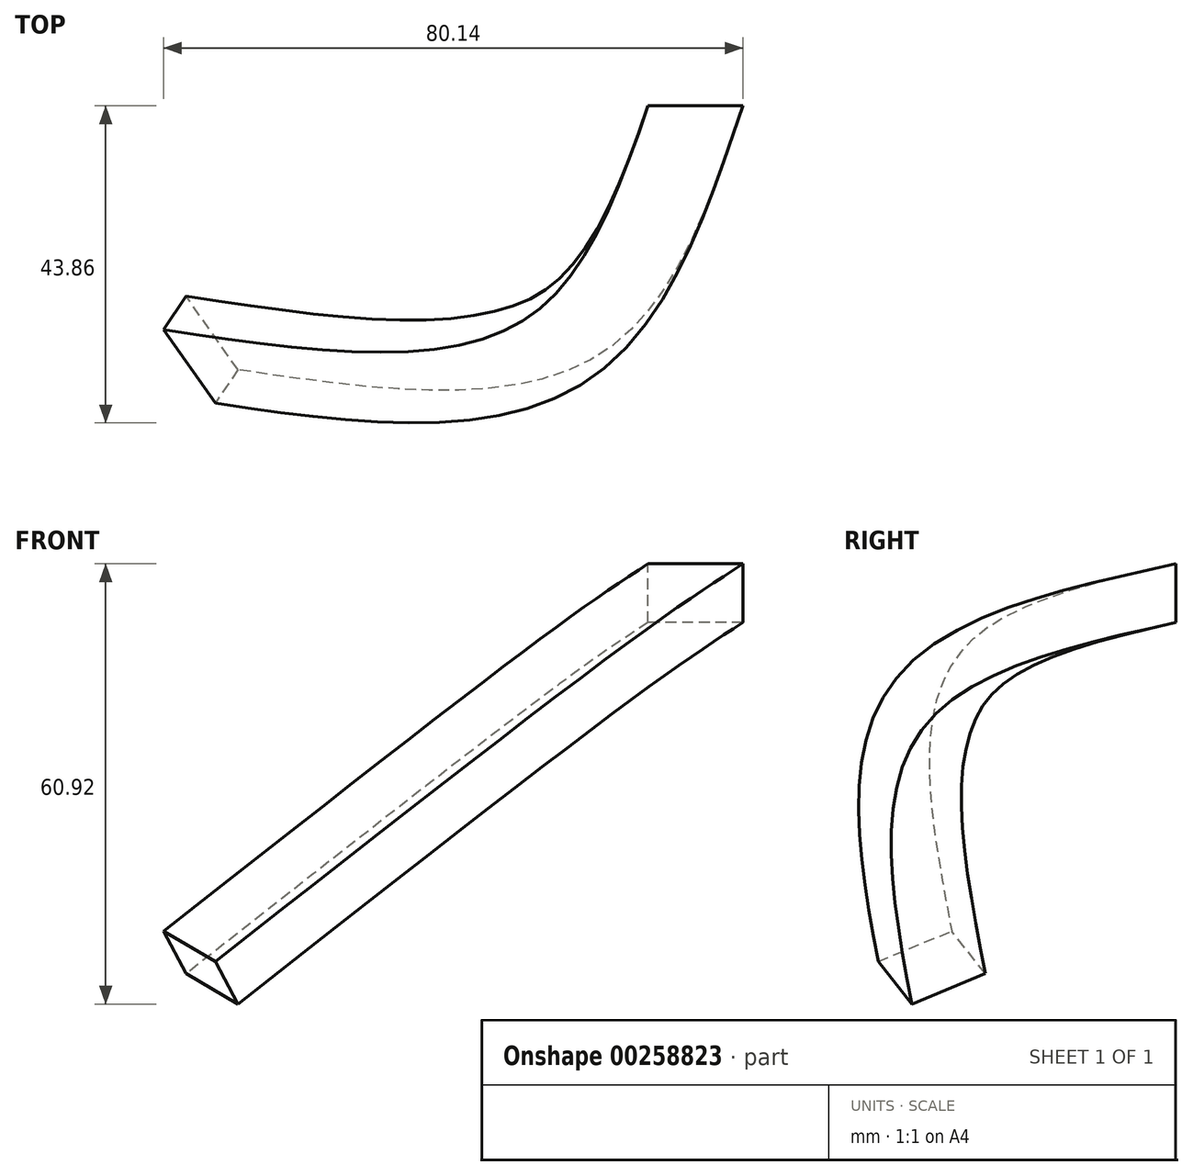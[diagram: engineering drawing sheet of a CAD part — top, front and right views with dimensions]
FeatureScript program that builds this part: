
annotation { "Feature Type Name" : "Feature", "Feature Type Description" : "" }
export const myFeature = defineFeature(function(context is Context, id is Id, definition is map)
    precondition{}
    {
        {
            var Q0;
            Q0=qCreatedBy(makeId("Front.planeOp"),FACE);
            var sketch = newSketch(context, id + "F0", { "sketchPlane" : qUnion([Q0])});
            skLineSegment(sketch, "E0.bottom", {"start": v(24.35, 47.76) * mm, "end": v(11.24, 47.76) * mm});
            skLineSegment(sketch, "E0.top", {"start": v(24.35, 55.88) * mm, "end": v(11.24, 55.88) * mm});
            skLineSegment(sketch, "E0.left", {"start": v(24.35, 47.76) * mm, "end": v(24.35, 55.88) * mm});
            skLineSegment(sketch, "E0.right", {"start": v(11.24, 47.76) * mm, "end": v(11.24, 55.88) * mm});
            skPoint(sketch, "E0.middle", {"position": v(17.8, 51.82) * mm});
            skSolve(sketch);
        }
        {
            var Q0;
            Q0=qCreatedBy(makeId("Top.planeOp"),FACE);
            var sketch = newSketch(context, id + "F1", { "sketchPlane" : qUnion([Q0])});
            skLineSegment(sketch, "E1.bottom", {"start": v(-38.98, -44.16) * mm, "end": v(-62.32, -44.16) * mm});
            skLineSegment(sketch, "E1.top", {"start": v(-38.98, -23.34) * mm, "end": v(-62.32, -23.34) * mm});
            skLineSegment(sketch, "E1.left", {"start": v(-38.98, -44.16) * mm, "end": v(-38.98, -23.34) * mm});
            skLineSegment(sketch, "E1.right", {"start": v(-62.32, -44.16) * mm, "end": v(-62.32, -23.34) * mm});
            skPoint(sketch, "E1.middle", {"position": v(-50.65, -33.75) * mm});
            skSolve(sketch);
        }
        {
            var Q0;
            Q0=qCreatedBy(makeId("Right.planeOp"),FACE);
            var sketch = newSketch(context, id + "F2", { "sketchPlane" : qUnion([Q0])});
            skPoint(sketch, "E2", {"position": v(-31.53, 39.34) * mm});
            skSolve(sketch);
        }
        {
            var Q0;
            Q0=sQuery(id+"F0.wireOp",VERTEX,"E0.middle");
            var Q1;
            Q1=sQuery(id+"F2.wireOp",VERTEX,"E2");
            var Q2;
            Q2=sQuery(id+"F1.wireOp",VERTEX,"E1.middle");
            cPlane(context, id + "F3", {"entities" : qUnion([Q0, Q1, Q2]), "cplaneType" : CPlaneType.THREE_POINT, "offset" : 25.4 * mm, "width" : 152.4 * mm, "height" : 152.4 * mm});
        }
        {
            var Q0;
            Q0=qCreatedBy(id+"F3.planeOp",FACE);
            var sketch = newSketch(context, id + "F4", { "sketchPlane" : qUnion([Q0])});
            skPoint(sketch, "E3.0", {"position": v(45.83, -2.24) * mm});
            skPoint(sketch, "E4.0", {"position": v(23.29, -33.2) * mm});
            skPoint(sketch, "E5.0", {"position": v(-40.88, -33.72) * mm});
            skFitSpline(sketch, "E6", {"points": [v(45.83, -2.24) * mm, v(23.29, -33.2) * mm, v(-40.88, -33.72) * mm], "startDerivative": vector(-38.21, -86.32) * mm, "endDerivative": vector(-131.23, 18.87) * mm});
            skSolve(sketch);
        }
        {
            var Q0;
            Q0=makeQuery(id+"F0.imprint","IMPRINT",FACE,{"disambiguationData":[TD([[makeQuery(id+"F0.imprint","IMPRINT",EDGE,{"derivedFrom":sQuery(id+"F0.wireOp",EDGE,"E0.bottom")}),-1.0]])]});
            var Q1;
            Q1=sQuery(id+"F4.wireOp",EDGE,"E6");
            sweep(context, id + "F5", {"profiles" : qUnion([Q0]), "path" : qUnion([Q1])});
        }
    });
